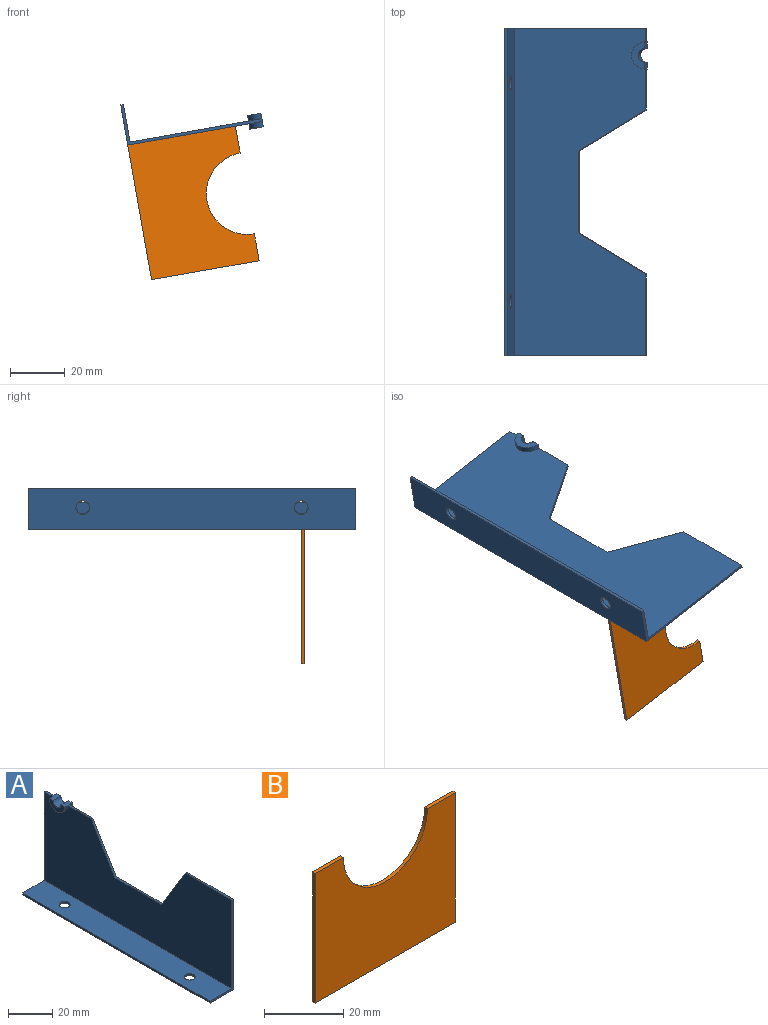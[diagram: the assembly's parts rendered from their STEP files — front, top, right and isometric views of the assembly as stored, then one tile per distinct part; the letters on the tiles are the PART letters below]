
ASSEMBLY  parts=2 mates=1
PART A: 20 faces, bbox 17x120x50 mm
  f0: plane 17.5x5mm, normal (0,0,1), area 27.5mm2, adj f2,f3,f10,f15,f16,f17,f18,f19
  f1: plane 7.5x5mm, normal (0,0,1), area 17.5mm2, adj f2,f3,f9,f15,f16,f17,f18,f19
  f2: plane 120x50mm, normal (1,0,0), area 4835.7mm2, adj f0,f1,f4,f7,f8,f9,f10,f11
  f3: plane 120x49mm, normal (-1,0,0), area 4715.7mm2, adj f0,f1,f4,f5,f8,f9,f10,f11
  f4: plane 30x1mm, normal (0,0,1), area 30mm2, adj f2,f3,f8,f11
  f5: plane 120x14mm, normal (0,0,1), area 1640.7mm2, adj f3,f6,f8,f9,f13,f14
  f6: plane 120x1mm, normal (-1,0,0), area 120mm2, adj f5,f7,f8,f9
  f7: plane 120x15mm, normal (0,0,-1), area 1760.7mm2, adj f2,f6,f8,f9,f13,f14
  f8: plane 50x15mm, normal (0,-1,0), area 64mm2, adj f2,f3,f4,f5,f6,f7
  f9: plane 50x15mm, normal (0,1,0), area 64mm2, adj f1,f2,f3,f5,f6,f7
  f10: plane 25x15mm, normal (0,-0.86,0.51), area 29.2mm2, adj f0,f2,f3,f12
  f11: plane 25x15mm, normal (0,0.86,0.51), area 29.2mm2, adj f2,f3,f4,f12
  f12: plane 30x1mm, normal (0,0,1), area 30mm2, adj f2,f3,f10,f11
  f13: cylinder r=2.5mm len=5mm, axis (0,0,-1), area 15.7mm2, adj f5,f7
  f14: cylinder r=2.5mm len=5mm, axis (0,0,-1), area 15.7mm2, adj f5,f7
  f15: plane 10x5mm, normal (-1,0,0), area 29.5mm2, adj f0,f1,f16,f17
  f16: cylinder r=5mm len=10mm, axis (-1,0,0), area 31.4mm2, adj f0,f1,f3,f15
  f17: cylinder r=2.5mm len=5mm, axis (-1,0,0), area 39.3mm2, adj f0,f1,f15,f19
  f18: cylinder r=5mm len=10mm, axis (-1,0,0), area 31.4mm2, adj f0,f1,f2,f19
  f19: plane 10x5mm, normal (1,0,0), area 29.5mm2, adj f0,f1,f17,f18
PART B: 8 faces, bbox 50x1x40 mm
  f0: plane 40x1mm, normal (-1,0,0), area 40mm2, adj f1,f5,f6,f7
  f1: plane 50x1mm, normal (0,0,-1), area 50mm2, adj f0,f2,f6,f7
  f2: plane 40x1mm, normal (1,0,0), area 40mm2, adj f1,f3,f6,f7
  f3: plane 10x1mm, normal (0,0,1), area 10mm2, adj f2,f4,f6,f7
  f4: cylinder r=15mm len=30mm, axis (0,1,0), area 47.1mm2, adj f3,f5,f6,f7
  f5: plane 10x1mm, normal (0,0,1), area 10mm2, adj f0,f4,f6,f7
  f6: plane 50x40mm, normal (0,-1,0), area 1646.6mm2, adj f0,f1,f2,f3,f4,f5
  f7: plane 50x40mm, normal (0,1,0), area 1646.6mm2, adj f0,f1,f2,f3,f4,f5
PLACE A rot(axis=(0,1,0),80deg) t=(-187.84,-49.71,102.3)mm fixed
PLACE B rot(axis=(0,1,0),80deg) t=(-183.41,-90.21,77.19)mm
MATE fastened B.f1 <-> A.f7  axis (0.98,0,0.17) through (-187.75,-89.71,101.81)mm
